# Revit family: HD032-2016.02.29-BT- Cielo 84R
name_source: partatom
category: Generic Models
revit_build: Autodesk Revit 2016 (Build: 20150714_1515(x64)
units: mm (PartAtom-declared; Revit-internal decimal feet)

## family parameters
Always vertical = Yes
Can host rebar = No
Cut with Voids When Loaded = No
Part Type = Normal
Room Calculation Point = No
Round Connector Dimension = Use Diameter
Shared = No
Work Plane-Based = No

## types (1)
- Productos HD
    AISLACION = <By Category>
    BT_Alto = 791
    BT_Ancho = 1400
    BT_Codigo_Origen = HD034
    BT_Color = 100 colores a eleccion
    BT_Descripcion = Cielo 84R/V5
    BT_EETT = Cielo 84R/V5
    BT_Elemento = Cielos
    BT_Especialidad = Estructura
    BT_Fabricante = Hunter Douglas
    BT_Itemizado_Estandar_CDT = D 04 04 80
    BT_Linea = De Linea
    BT_Marca = Hunter Douglas
    BT_MasterFormat® = 09 54 23
    BT_Material = Aluzinc
    BT_Nombre_Corto = Cielo 84R
    BT_Nombre_Tecnico = Cielo 84R/V5
    BT_Profundidad = Largo Máximo 6 mts
    BT_SKU = 00 00 00
    BT_Uso = Interior
    BT_Web_del_Producto = http://www.hunterdouglas.cl
    Distancia  entre apoyos = 1200 mm  [stored 3.93701 ft]
    ID_Objeto = BT_F_F_238
    ID_Source = BIMTOOL
    Largo Panel (Editar Largo en tipo de panel) = 1400 mm  [stored 4.59318 ft]
    Manufacturer = Hunter Douglas
    Material = Phase - Demo
    Poliuretano = <By Category>
    URL = http://www.hunterdouglas.cl

note: [stored X ft] marks values corroborated as IEEE doubles in the binary element streams (Revit-internal decimal feet)

## geometry (parser evidence)
native form markers: Blend x8, Sweep x37
no freeform markers — native parametric forms only
